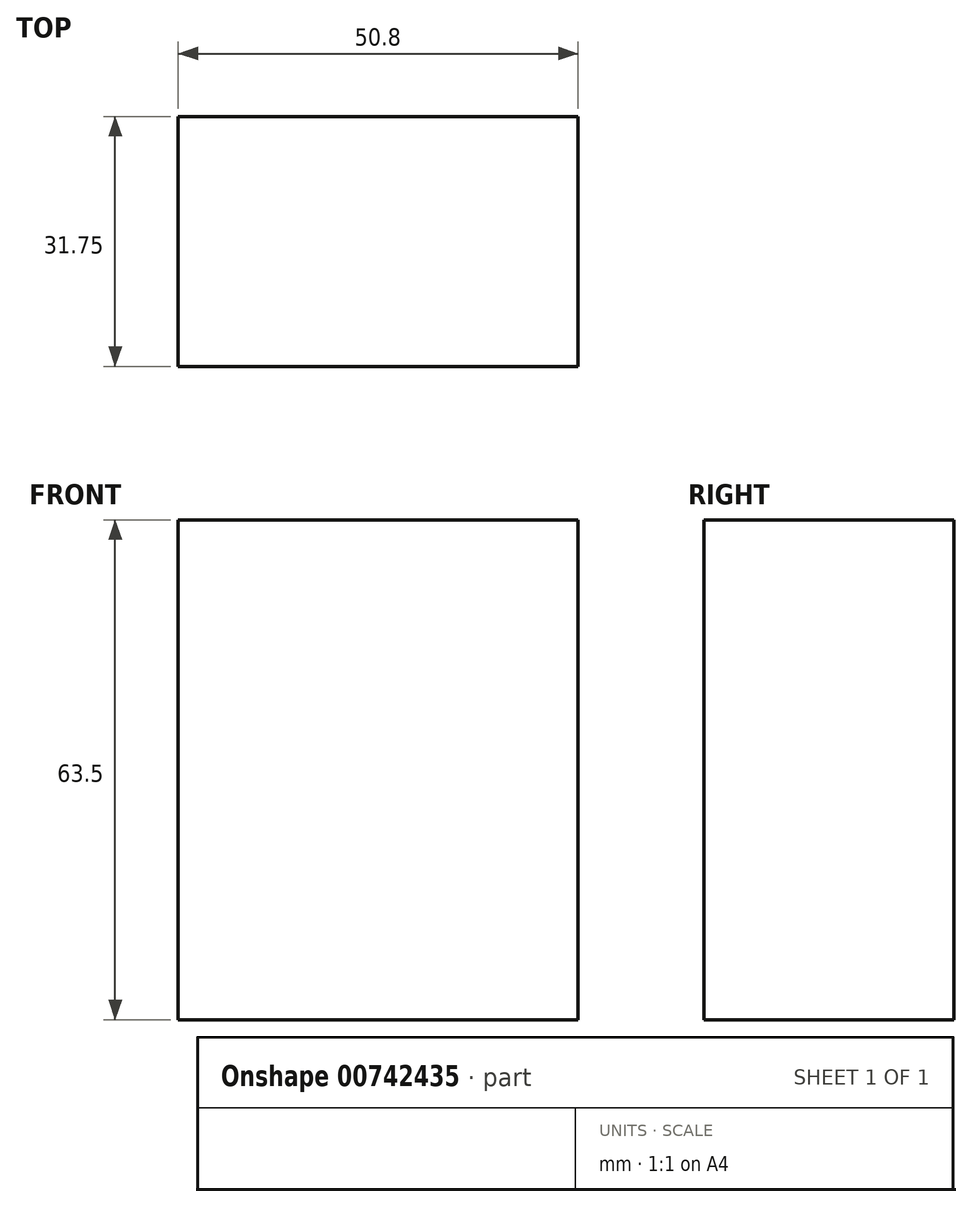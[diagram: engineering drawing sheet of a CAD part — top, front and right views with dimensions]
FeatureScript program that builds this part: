
annotation { "Feature Type Name" : "Feature", "Feature Type Description" : "" }
export const myFeature = defineFeature(function(context is Context, id is Id, definition is map)
    precondition{}
    {
        {
            var Q0;
            Q0=qCreatedBy(makeId("Front.planeOp"),FACE);
            var sketch = newSketch(context, id + "F0", { "sketchPlane" : qUnion([Q0])});
            skLineSegment(sketch, "E0", {"start": v(0, 0) * mm, "end": v(0, 63.5) * mm});
            skLineSegment(sketch, "E1", {"start": v(0, 63.5) * mm, "end": v(50.8, 63.5) * mm});
            skLineSegment(sketch, "E2", {"start": v(50.8, 63.5) * mm, "end": v(50.8, 0) * mm});
            skLineSegment(sketch, "E3", {"start": v(50.8, 0) * mm, "end": v(0, 0) * mm});
            skSolve(sketch);
        }
        {
            var Q0;
            Q0 = qSketchRegion(id + "F0", true);
            extrude(context, id + "F1", {"entities" : qUnion([Q0]), "depth" : 31.75 * mm, "offsetDistance" : 25.4 * mm});
        }
    });
